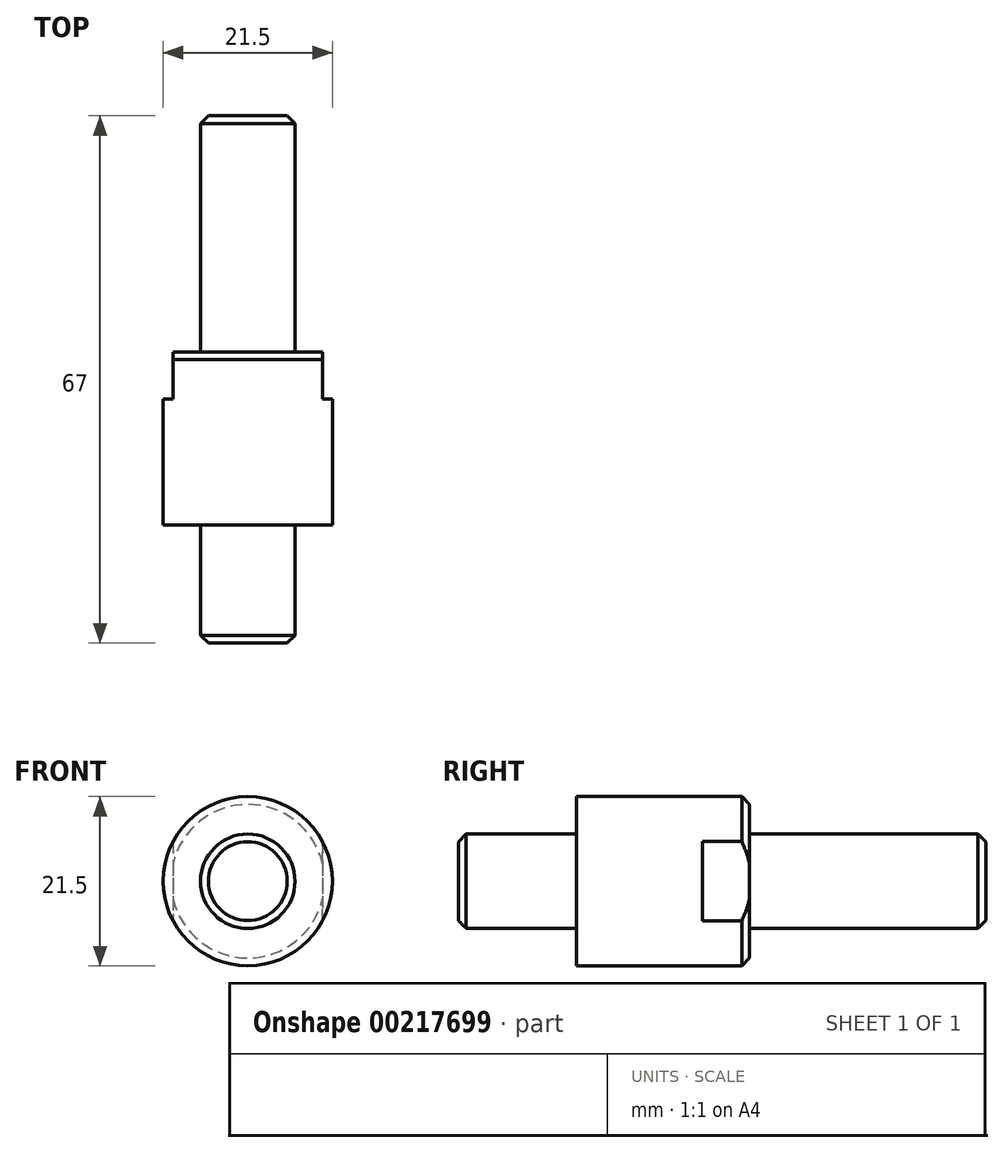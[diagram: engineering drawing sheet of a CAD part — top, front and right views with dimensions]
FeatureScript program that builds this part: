
annotation { "Feature Type Name" : "Feature", "Feature Type Description" : "" }
export const myFeature = defineFeature(function(context is Context, id is Id, definition is map)
    precondition{}
    {
        {
            var Q0;
            Q0=qCreatedBy(makeId("Front.planeOp"),FACE);
            var sketch = newSketch(context, id + "F0", { "sketchPlane" : qUnion([Q0])});
            skCircle(sketch, "E0", {"center": v(0, 0) * mm, "radius": 6 * mm});
            skSolve(sketch);
        }
        {
            var Q0;
            Q0 = qSketchRegion(id + "F0", true);
            extrude(context, id + "F1", {"entities" : qUnion([Q0]), "depth" : 67 * mm});
        }
        {
            var Q0;
            Q0=makeQuery(id+"F1.opExtrude","CAP_FACE",FACE,{"disambiguationData":[OSD([sQuery(id+"F0.wireOp",EDGE,"E0")])],"isStart":false});
            cPlane(context, id + "F2", {"entities" : qUnion([Q0]), "cplaneType" : CPlaneType.OFFSET, "offset" : 15 * mm, "oppositeDirection" : true, "width" : 150 * mm, "height" : 150 * mm});
        }
        {
            var Q0;
            Q0=qCreatedBy(id+"F2.planeOp",FACE);
            var sketch = newSketch(context, id + "F3", { "sketchPlane" : qUnion([Q0])});
            skCircle(sketch, "E1", {"center": v(0, 0) * mm, "radius": 10.75 * mm});
            skSolve(sketch);
        }
        {
            var Q0;
            Q0 = qSketchRegion(id + "F3", true);
            extrude(context, id + "F4", {"entities" : qUnion([Q0]), "operationType" : NewBodyOperationType.ADD, "oppositeDirection" : true, "depth" : 22 * mm});
        }
        {
            var Q0;
            Q0=makeQuery(id+"F4.opExtrude","CAP_FACE",FACE,{"disambiguationData":[OSD([sQuery(id+"F3.wireOp",EDGE,"E1")])],"isStart":false});
            var sketch = newSketch(context, id + "F5", { "sketchPlane" : qUnion([Q0])});
            skLineSegment(sketch, "E2.bottom", {"start": v(-9.5, 12.2) * mm, "end": v(9.5, 12.2) * mm});
            skLineSegment(sketch, "E2.top", {"start": v(-9.5, -12.5) * mm, "end": v(9.5, -12.5) * mm});
            skLineSegment(sketch, "E2.left", {"start": v(-9.5, 12.2) * mm, "end": v(-9.5, -12.5) * mm});
            skLineSegment(sketch, "E2.right", {"start": v(9.5, 12.2) * mm, "end": v(9.5, -12.5) * mm});
            skLineSegment(sketch, "E3.bottom", {"start": v(-14.13, 15.46) * mm, "end": v(12.36, 15.46) * mm});
            skLineSegment(sketch, "E3.top", {"start": v(-14.13, -16.34) * mm, "end": v(12.36, -16.34) * mm});
            skLineSegment(sketch, "E3.left", {"start": v(-14.13, 15.46) * mm, "end": v(-14.13, -16.34) * mm});
            skLineSegment(sketch, "E3.right", {"start": v(12.36, 15.46) * mm, "end": v(12.36, -16.34) * mm});
            skSolve(sketch);
        }
        {
            var Q0;
            Q0 = qSketchRegion(id + "F5", true);
            extrude(context, id + "F6", {"entities" : qUnion([Q0]), "operationType" : NewBodyOperationType.REMOVE, "oppositeDirection" : true, "depth" : 6 * mm});
        }
        {
            var Q0;
            Q0=makeQuery(id+"F1.opExtrude","CAP_EDGE",EDGE,{"disambiguationData":[OSD([sQuery(id+"F0.wireOp",EDGE,"E0")])],"isStart":false});
            var Q1;
            Q1=makeQuery(id+"F1.opExtrude","CAP_EDGE",EDGE,{"disambiguationData":[OSD([sQuery(id+"F0.wireOp",EDGE,"E0")])],"isStart":true});
            var Q2;
            Q2=makeQuery(id+"F6.boolean.opBoolean","SPLIT",EDGE,{"disambiguationData":[OD(1.0)],"derivedFrom":makeQuery(id+"F4.opExtrude","CAP_EDGE",EDGE,{"disambiguationData":[OSD([sQuery(id+"F3.wireOp",EDGE,"E1")])],"isStart":false})});
            var Q3;
            Q3=makeQuery(id+"F6.boolean.opBoolean","SPLIT",EDGE,{"disambiguationData":[OD(0.0)],"derivedFrom":makeQuery(id+"F4.opExtrude","CAP_EDGE",EDGE,{"disambiguationData":[OSD([sQuery(id+"F3.wireOp",EDGE,"E1")])],"isStart":false})});
            chamfer(context, id + "F7", {"entities" : qUnion([Q0, Q1, Q2, Q3]), "width" : 1 * mm, "tangentPropagation" : true});
        }
    });
